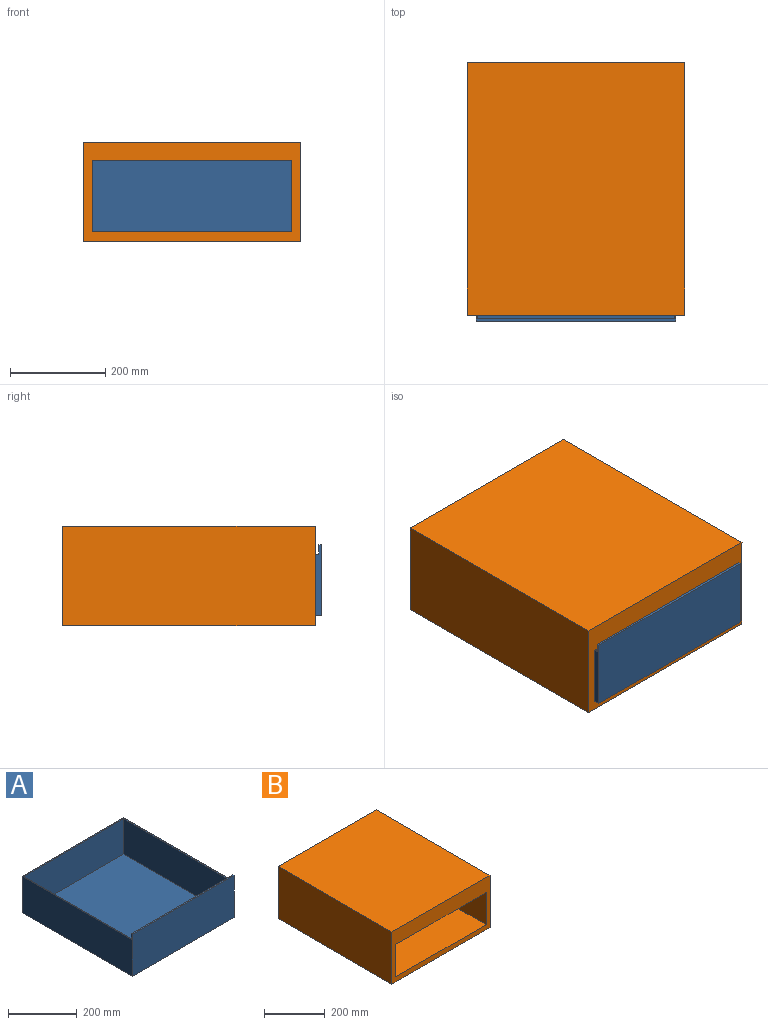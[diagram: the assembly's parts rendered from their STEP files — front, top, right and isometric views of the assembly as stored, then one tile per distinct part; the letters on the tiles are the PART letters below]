
ASSEMBLY  parts=2 mates=1
PART A: 12 faces, bbox 420x455x150 mm
  f0: plane 420x130mm, normal (0,1,0), area 54600mm2, adj f1,f2,f3,f4
  f1: plane 455x150mm, normal (-1,0,0), area 59250mm2, adj f0,f3,f4,f9,f10,f11
  f2: plane 455x150mm, normal (1,0,0), area 59250mm2, adj f0,f3,f4,f9,f10,f11
  f3: plane 450x420mm, normal (0,0,1), area 5248mm2, adj f0,f1,f2,f5,f6,f7,f11
  f4: plane 455x420mm, normal (0,0,-1), area 191100mm2, adj f0,f1,f2,f10
  f5: plane 446x126mm, normal (-1,0,0), area 56196mm2, adj f3,f6,f8,f11
  f6: plane 412x126mm, normal (0,-1,0), area 51912mm2, adj f3,f5,f7,f8
  f7: plane 446x126mm, normal (1,0,0), area 56196mm2, adj f3,f6,f8,f11
  f8: plane 446x412mm, normal (0,0,1), area 183752mm2, adj f5,f6,f7,f11
  f9: plane 420x5mm, normal (0,0,1), area 2100mm2, adj f1,f2,f10,f11
  f10: plane 420x150mm, normal (0,-1,0), area 63000mm2, adj f1,f2,f4,f9
  f11: plane 420x146mm, normal (0,1,0), area 60312mm2, adj f1,f2,f3,f5,f7,f8,f9
PART B: 11 faces, bbox 456x530x210 mm
  f0: plane 456x210mm, normal (0,-1,0), area 41160mm2, adj f1,f3,f4,f5,f6,f7,f8,f9
  f1: plane 530x210mm, normal (1,0,0), area 111300mm2, adj f0,f2,f4,f5
  f2: plane 456x210mm, normal (0,1,0), area 95760mm2, adj f1,f3,f4,f5
  f3: plane 530x210mm, normal (-1,0,0), area 111300mm2, adj f0,f2,f4,f5
  f4: plane 530x456mm, normal (0,0,1), area 241680mm2, adj f0,f1,f2,f3
  f5: plane 530x456mm, normal (0,0,-1), area 241680mm2, adj f0,f1,f2,f3
  f6: plane 450x420mm, normal (0,0,-1), area 189000mm2, adj f0,f7,f9,f10
  f7: plane 450x130mm, normal (1,0,0), area 58500mm2, adj f0,f6,f8,f10
  f8: plane 450x420mm, normal (0,0,1), area 189000mm2, adj f0,f7,f9,f10
  f9: plane 450x130mm, normal (-1,0,0), area 58500mm2, adj f0,f6,f8,f10
  f10: plane 420x130mm, normal (0,-1,0), area 54600mm2, adj f6,f7,f8,f9
PLACE A t=(1299.22,20.66,101.78)mm
PLACE B t=(341.58,-134.96,80.78)mm
MATE slider A.f10 <-> B.f0  axis (0,-1,0) through (341.58,-412.86,101.78)mm
